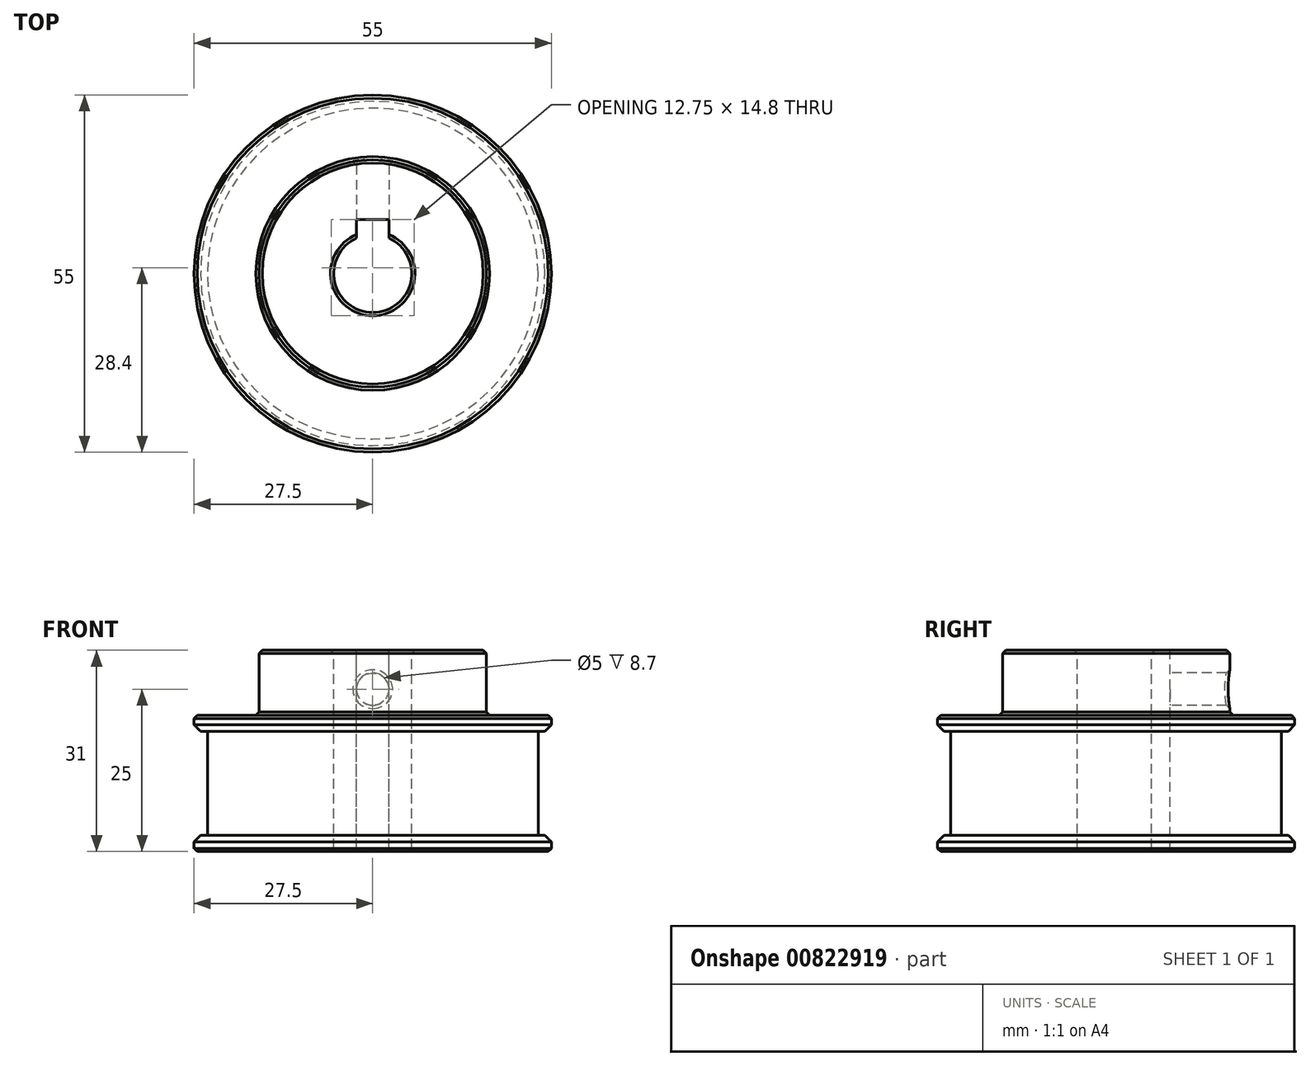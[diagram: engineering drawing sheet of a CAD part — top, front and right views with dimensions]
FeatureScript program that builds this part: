
annotation { "Feature Type Name" : "Feature", "Feature Type Description" : "" }
export const myFeature = defineFeature(function(context is Context, id is Id, definition is map)
    precondition{}
    {
        {
            var Q0;
            Q0=qCreatedBy(makeId("Front.planeOp"),FACE);
            var sketch = newSketch(context, id + "F0", { "sketchPlane" : qUnion([Q0])});
            skLineSegment(sketch, "E0", {"start": v(0, 38.23) * mm, "end": v(0, 0) * mm, "construction": true});
            skLineSegment(sketch, "E1", {"start": v(0, 0) * mm, "end": v(-6, 0) * mm, "construction": true});
            skLineSegment(sketch, "E2", {"start": v(-6, 0) * mm, "end": v(-6, 31) * mm});
            skLineSegment(sketch, "E3", {"start": v(-6, 31) * mm, "end": v(-17.5, 31) * mm});
            skLineSegment(sketch, "E4", {"start": v(-17.5, 31) * mm, "end": v(-17.5, 21) * mm});
            skLineSegment(sketch, "E5", {"start": v(-17.5, 21) * mm, "end": v(-27.5, 21) * mm});
            skLineSegment(sketch, "E6", {"start": v(-27.5, 21) * mm, "end": v(-27.5, 18.5) * mm});
            skLineSegment(sketch, "E7", {"start": v(-27.5, 18.5) * mm, "end": v(-25.46, 18.5) * mm});
            skLineSegment(sketch, "E8", {"start": v(-25.46, 18.5) * mm, "end": v(-25.46, 2.5) * mm});
            skLineSegment(sketch, "E9", {"start": v(-25.46, 2.5) * mm, "end": v(-27.5, 2.5) * mm});
            skLineSegment(sketch, "E10", {"start": v(-27.5, 2.5) * mm, "end": v(-27.5, 0) * mm});
            skLineSegment(sketch, "E11", {"start": v(-27.5, 0) * mm, "end": v(-6, 0) * mm});
            skSolve(sketch);
        }
        {
            var Q0;
            Q0 = qSketchRegion(id + "F0", true);
            var Q1;
            Q1=sQuery(id+"F0.wireOp",EDGE,"E0");
            revolve(context, id + "F1", {"surfaceOperationType" : NewSurfaceOperationType.NEW, "entities" : qUnion([Q0]), "axis" : qUnion([Q1]), "revolveType" : RevolveType.FULL});
        }
        {
            var Q0;
            Q0=makeQuery(id+"F1.opRevolve","SWEPT_EDGE",EDGE,{"disambiguationData":[OSD([sQuery(id+"F0.wireOp",EDGE,"E9"),sQuery(id+"F0.wireOp",EDGE,"E10")])]});
            var Q1;
            Q1=makeQuery(id+"F1.opRevolve","SWEPT_EDGE",EDGE,{"disambiguationData":[OSD([sQuery(id+"F0.wireOp",EDGE,"E6"),sQuery(id+"F0.wireOp",EDGE,"E7")])]});
            chamfer(context, id + "F2", {"entities" : qUnion([Q0, Q1]), "width" : 1 * mm, "tangentPropagation" : true});
        }
        {
            var Q0;
            Q0=makeQuery(id+"F1.opRevolve","SWEPT_FACE",FACE,{"disambiguationData":[OSD([sQuery(id+"F0.wireOp",EDGE,"E5")])]});
            var Q1;
            Q1=makeQuery(id+"F1.opRevolve","SWEPT_FACE",FACE,{"disambiguationData":[OSD([sQuery(id+"F0.wireOp",EDGE,"E3")])]});
            var Q2;
            Q2=makeQuery(id+"F1.opRevolve","SWEPT_FACE",FACE,{"disambiguationData":[OSD([sQuery(id+"F0.wireOp",EDGE,"E11")])]});
            chamfer(context, id + "F3", {"entities" : qUnion([Q0, Q1, Q2]), "width" : 0.5 * mm, "tangentPropagation" : true});
        }
        {
            var Q0;
            Q0=makeQuery(id+"F1.opRevolve","SWEPT_FACE",FACE,{"disambiguationData":[OSD([sQuery(id+"F0.wireOp",EDGE,"E3")])]});
            var sketch = newSketch(context, id + "F4", { "sketchPlane" : qUnion([Q0])});
            skLineSegment(sketch, "E12", {"start": v(0, 0) * mm, "end": v(0, 5.8) * mm, "construction": true});
            skLineSegment(sketch, "E13.bottom", {"start": v(-2.5, 3.3) * mm, "end": v(2.5, 3.3) * mm});
            skLineSegment(sketch, "E13.top", {"start": v(-2.5, 8.3) * mm, "end": v(2.5, 8.3) * mm});
            skLineSegment(sketch, "E13.left", {"start": v(-2.5, 3.3) * mm, "end": v(-2.5, 8.3) * mm});
            skLineSegment(sketch, "E13.right", {"start": v(2.5, 3.3) * mm, "end": v(2.5, 8.3) * mm});
            skPoint(sketch, "E13.middle", {"position": v(0, 5.8) * mm});
            skCircle(sketch, "E14.0", {"center": v(0, 0) * mm, "radius": 6 * mm, "construction": true});
            skPoint(sketch, "E15", {"position": v(0, -6) * mm});
            skSolve(sketch);
        }
        {
            var Q0;
            Q0 = qSketchRegion(id + "F4", true);
            var Q1;
            Q1=makeQuery(id+"F1.opRevolve","SWEPT_FACE",FACE,{"disambiguationData":[OSD([sQuery(id+"F0.wireOp",EDGE,"E11")])]});
            extrude(context, id + "F5", {"entities" : qUnion([Q0]), "operationType" : NewBodyOperationType.REMOVE, "endBound" : BoundingType.UP_TO_SURFACE, "oppositeDirection" : true, "depth" : 25 * mm, "endBoundEntityFace" : qUnion([Q1]), "offsetDistance" : 25 * mm});
        }
        {
            var Q0;
            Q0=qCreatedBy(makeId("Front.planeOp"),FACE);
            var sketch = newSketch(context, id + "F6", { "sketchPlane" : qUnion([Q0])});
            skLineSegment(sketch, "E16", {"start": v(0, 0) * mm, "end": v(0, 25) * mm, "construction": true});
            skCircle(sketch, "E17", {"center": v(0, 25) * mm, "radius": 2.5 * mm});
            skSolve(sketch);
        }
        {
            var Q0;
            Q0 = qSketchRegion(id + "F6", true);
            extrude(context, id + "F7", {"entities" : qUnion([Q0]), "operationType" : NewBodyOperationType.REMOVE, "oppositeDirection" : true, "depth" : 25 * mm, "offsetDistance" : 25 * mm});
        }
        {
            var Q0;
            Q0=makeQuery(id+"F7.boolean.opBoolean","INTERSECT",EDGE,{"derivedFrom":[makeQuery(id+"F1.opRevolve","SWEPT_FACE",FACE,{"disambiguationData":[OSD([sQuery(id+"F0.wireOp",EDGE,"E4")])]}),makeQuery(id+"F7.opExtrude","SWEPT_FACE",FACE,{"disambiguationData":[OSD([sQuery(id+"F6.wireOp",EDGE,"E17")])]})]});
            chamfer(context, id + "F8", {"entities" : qUnion([Q0]), "width" : 0.5 * mm, "tangentPropagation" : true});
        }
    });
